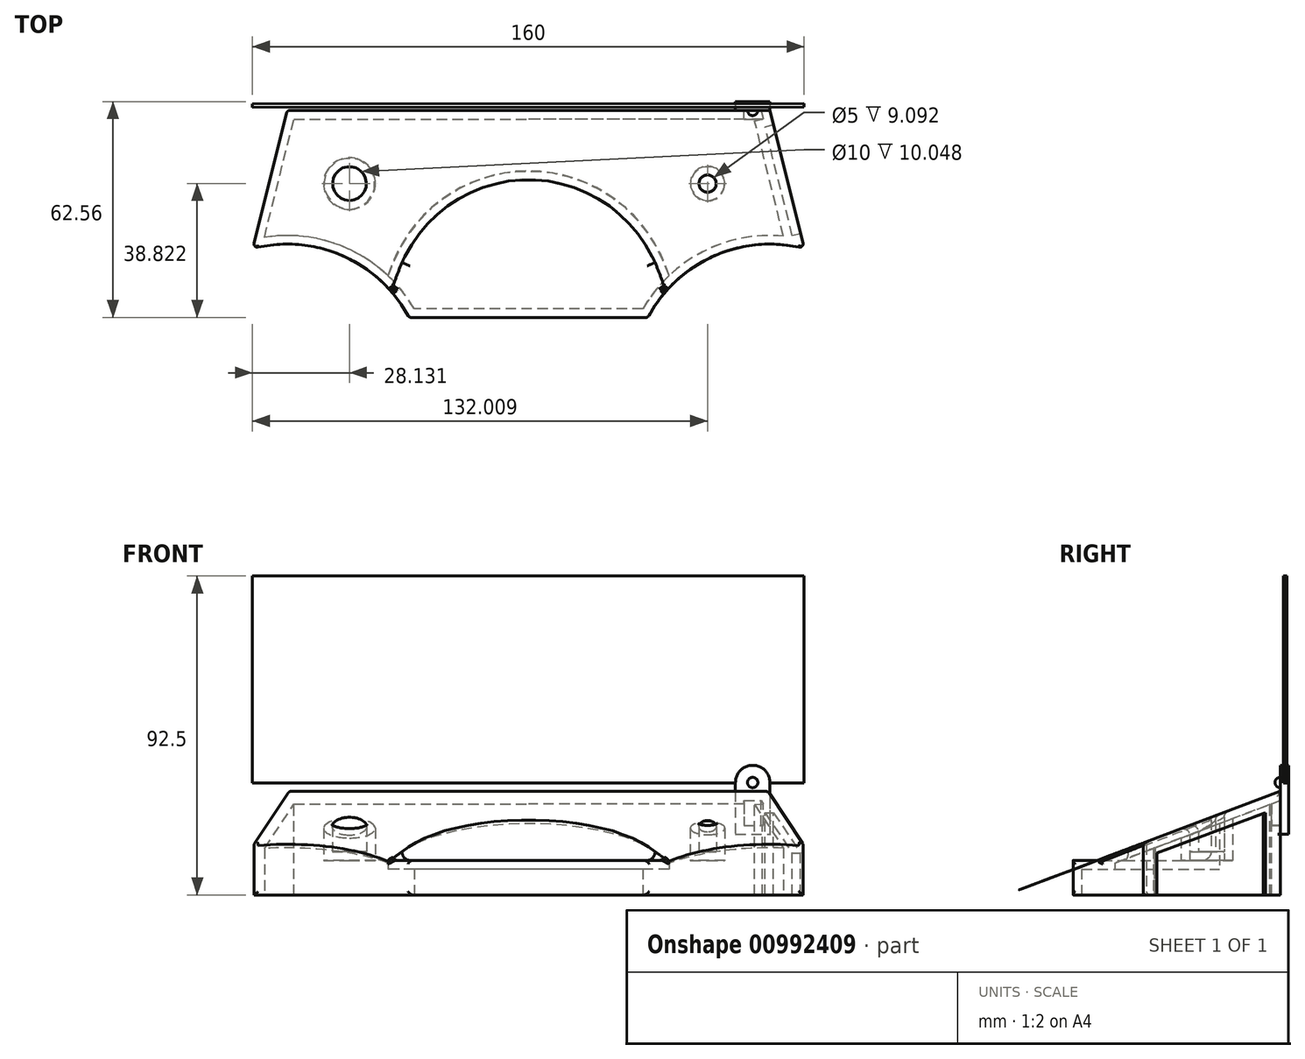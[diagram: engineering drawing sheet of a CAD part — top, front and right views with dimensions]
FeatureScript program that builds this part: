
annotation { "Feature Type Name" : "Feature", "Feature Type Description" : "" }
export const myFeature = defineFeature(function(context is Context, id is Id, definition is map)
    precondition{}
    {
        {
            var Q0;
            Q0=qCreatedBy(makeId("Top.planeOp"),FACE);
            var sketch = newSketch(context, id + "F0", { "sketchPlane" : qUnion([Q0])});
            skLineSegment(sketch, "E0.left", {"start": v(-80, 40) * mm, "end": v(-70, 80.06) * mm});
            skLineSegment(sketch, "E1", {"start": v(0, 0) * mm, "end": v(0, 40) * mm});
            skLineSegment(sketch, "E2", {"start": v(0, 0) * mm, "end": v(0, 80) * mm});
            skLineSegment(sketch, "E3", {"start": v(-70, 80.06) * mm, "end": v(0, 80) * mm});
            skLineSegment(sketch, "E4.MirrorCS", {"start": v(70, 80.06) * mm, "end": v(0, 80) * mm});
            skLineSegment(sketch, "E5.MirrorCS", {"start": v(80, 40) * mm, "end": v(70, 80.06) * mm});
            skCircle(sketch, "E6", {"center": v(0, 40) * mm, "radius": 40 * mm});
            skLineSegment(sketch, "E7", {"start": v(0, 40) * mm, "end": v(0, 0) * mm});
            skLineSegment(sketch, "E8", {"start": v(0, 20) * mm, "end": v(-34.64, 20) * mm});
            skLineSegment(sketch, "E9", {"start": v(-34.64, 20) * mm, "end": v(34.64, 20) * mm});
            skArc(sketch, "E10", {"start": v(-34.64, 20) * mm, "mid": v(-53.85, 37.87) * mm, "end": v(-80, 40) * mm});
            skArc(sketch, "E11", {"start": v(80, 40) * mm, "mid": v(53.85, 37.87) * mm, "end": v(34.64, 20) * mm});
            skSolve(sketch);
        }
        {
            var Q0;
            Q0=makeQuery(id+"F0.imprint","IMPRINT",FACE,{"disambiguationData":[TD([[makeQuery(id+"F0.imprint","IMPRINT",EDGE,{"derivedFrom":sQuery(id+"F0.wireOp",EDGE,"E0.left")}),-1.0]])]});
            var Q1;
            {var subQ0=sQuery(id+"F0.wireOp",EDGE,"E4.MirrorCS");Q1=makeQuery(id+"F0.imprint","IMPRINT",FACE,{"disambiguationData":[TD([[makeQuery(id+"F0.imprint","IMPRINT",EDGE,{"derivedFrom":subQ0}),1.0]])]});}
            var Q2;
            {var subQ6=sQuery(id+"F0.wireOp",EDGE,"E2");Q2=makeQuery(id+"F0.imprint","IMPRINT",FACE,{"disambiguationData":[TD([[makeQuery(id+"F0.imprint","IMPRINT",EDGE,{"derivedFrom":subQ6}),1.0]])]});}
            var Q3;
            {var subQ0=sQuery(id+"F0.wireOp",EDGE,"E7");var subQ1=sQuery(id+"F0.wireOp",EDGE,"E6");var subQ2=makeQuery(id+"F0.imprint","INTERSECT",VERTEX,{"derivedFrom":[subQ1,subQ0]});Q3=makeQuery(id+"F0.imprint","IMPRINT",FACE,{"disambiguationData":[TD([[makeQuery(id+"F0.imprint","IMPRINT",EDGE,{"disambiguationData":[TD([[subQ2,1.0]])],"derivedFrom":subQ0}),-1.0]])]});}
            var Q4;
            {var subQ6=sQuery(id+"F0.wireOp",EDGE,"E2");Q4=makeQuery(id+"F0.imprint","IMPRINT",FACE,{"disambiguationData":[TD([[makeQuery(id+"F0.imprint","IMPRINT",EDGE,{"derivedFrom":subQ6}),-1.0]])]});}
            var Q5;
            {var subQ0=sQuery(id+"F0.wireOp",EDGE,"E7");var subQ1=sQuery(id+"F0.wireOp",EDGE,"E6");var subQ2=makeQuery(id+"F0.imprint","INTERSECT",VERTEX,{"derivedFrom":[subQ1,subQ0]});Q5=makeQuery(id+"F0.imprint","IMPRINT",FACE,{"disambiguationData":[TD([[makeQuery(id+"F0.imprint","IMPRINT",EDGE,{"disambiguationData":[TD([[subQ2,1.0]])],"derivedFrom":subQ0}),1.0]])]});}
            extrude(context, id + "F1", {"entities" : qUnion([Q0, Q1, Q2, Q3, Q4, Q5]), "depth" : 30 * mm, "offsetDistance" : 25 * mm});
        }
        {
            var Q0;
            Q0=qCreatedBy(makeId("Right.planeOp"),FACE);
            var sketch = newSketch(context, id + "F2", { "sketchPlane" : qUnion([Q0])});
            skLineSegment(sketch, "E12", {"start": v(0, 0) * mm, "end": v(0, 10) * mm});
            skLineSegment(sketch, "E13", {"start": v(0, 10) * mm, "end": v(40, 10) * mm});
            skLineSegment(sketch, "E14", {"start": v(40, 10) * mm, "end": v(40, 30) * mm});
            skLineSegment(sketch, "E15", {"start": v(40, 30) * mm, "end": v(0, 30) * mm});
            skLineSegment(sketch, "E16", {"start": v(0, 30) * mm, "end": v(0, 10) * mm});
            skLineSegment(sketch, "E17", {"start": v(0, 30) * mm, "end": v(-10, 30) * mm});
            skLineSegment(sketch, "E18", {"start": v(-10, 30) * mm, "end": v(-10, 10) * mm});
            skLineSegment(sketch, "E19", {"start": v(-10, 10) * mm, "end": v(0, 10) * mm});
            skSolve(sketch);
        }
        {
            var Q0;
            Q0=qSketchRegion(id+"F2",true);
            extrude(context, id + "F3", {"entities" : qUnion([Q0]), "operationType" : NewBodyOperationType.REMOVE, "depth" : 10 * mm, "offsetDistance" : 25 * mm, "hasSecondDirection" : true, "secondDirectionOppositeDirection" : true, "secondDirectionDepth" : 10 * mm});
        }
        {
            var Q0;
            Q0=makeQuery(id+"F1.opExtrude","SWEPT_FACE",FACE,{"disambiguationData":[OSD([sQuery(id+"F0.wireOp",EDGE,"E4.MirrorCS")])]});
            var sketch = newSketch(context, id + "F4", { "sketchPlane" : qUnion([Q0])});
            skLineSegment(sketch, "E20", {"start": v(-0.08, 27.6) * mm, "end": v(-65.08, 27.6) * mm});
            skLineSegment(sketch, "E21.bottom", {"start": v(-65.08, 37.6) * mm, "end": v(-65.08, 37.6) * mm});
            skLineSegment(sketch, "E21.top", {"start": v(-60.08, 17.6) * mm, "end": v(-70.08, 17.6) * mm});
            skLineSegment(sketch, "E21.left", {"start": v(-60.08, 32.6) * mm, "end": v(-60.08, 17.6) * mm});
            skLineSegment(sketch, "E21.right", {"start": v(-70.08, 32.6) * mm, "end": v(-70.08, 17.6) * mm});
            skPoint(sketch, "E21.middle", {"position": v(-65.08, 27.6) * mm});
            skPoint(sketch, "E22.visualSharp", {"position": v(-60.08, 37.6) * mm});
            skArc(sketch, "E22.filletArc", {"start": v(-60.08, 32.6) * mm, "mid": v(-61.55, 36.14) * mm, "end": v(-65.08, 37.6) * mm});
            skPoint(sketch, "E23.visualSharp", {"position": v(-70.08, 37.6) * mm});
            skArc(sketch, "E23.filletArc", {"start": v(-65.08, 37.6) * mm, "mid": v(-68.62, 36.14) * mm, "end": v(-70.08, 32.6) * mm});
            skSolve(sketch);
        }
        {
            var Q0;
            Q0=qSketchRegion(id+"F4",true);
            extrude(context, id + "F5", {"entities" : qUnion([Q0]), "operationType" : NewBodyOperationType.ADD, "depth" : 2.5 * mm, "offsetDistance" : 25 * mm});
        }
        {
            var Q0;
            Q0=makeQuery(id+"F5.opExtrude","CAP_FACE",FACE,{"disambiguationData":[OSD([sQuery(id+"F4.wireOp",EDGE,"E21.top"),sQuery(id+"F4.wireOp",EDGE,"E21.left"),sQuery(id+"F4.wireOp",EDGE,"E21.right"),sQuery(id+"F4.wireOp",EDGE,"E22.filletArc"),sQuery(id+"F4.wireOp",EDGE,"E23.filletArc")])],"isStart":true});
            var sketch = newSketch(context, id + "F6", { "sketchPlane" : qUnion([Q0])});
            skArc(sketch, "E24", {"start": v(66.58, 32.6) * mm, "mid": v(65.08, 34.1) * mm, "end": v(63.58, 32.6) * mm});
            skLineSegment(sketch, "E25", {"start": v(66.58, 32.6) * mm, "end": v(63.58, 32.6) * mm});
            skSolve(sketch);
        }
        {
            var Q0;
            Q0=qSketchRegion(id+"F6",true);
            var Q1;
            Q1=sQuery(id+"F6.wireOp",EDGE,"E25");
            revolve(context, id + "F7", {"operationType" : NewBodyOperationType.ADD, "surfaceOperationType" : NewSurfaceOperationType.NEW, "entities" : qUnion([Q0]), "axis" : qUnion([Q1]), "revolveType" : RevolveType.FULL});
        }
        {
            var Q0;
            Q0=makeQuery(id+"F5.opExtrude","CAP_FACE",FACE,{"disambiguationData":[OSD([sQuery(id+"F4.wireOp",EDGE,"E21.top"),sQuery(id+"F4.wireOp",EDGE,"E21.left"),sQuery(id+"F4.wireOp",EDGE,"E21.right"),sQuery(id+"F4.wireOp",EDGE,"E22.filletArc"),sQuery(id+"F4.wireOp",EDGE,"E23.filletArc")])],"isStart":false});
            cPlane(context, id + "F8", {"entities" : qUnion([Q0]), "cplaneType" : CPlaneType.OFFSET, "offset" : 1 * mm, "oppositeDirection" : true, "width" : 150 * mm, "height" : 150 * mm});
        }
        {
            var Q0;
            Q0=qCreatedBy(id+"F8.planeOp",FACE);
            var sketch = newSketch(context, id + "F9", { "sketchPlane" : qUnion([Q0])});
            skLineSegment(sketch, "E26", {"start": v(0, 0) * mm, "end": v(0, 32.5) * mm});
            skLineSegment(sketch, "E27", {"start": v(0, 32.5) * mm, "end": v(-80, 32.5) * mm});
            skLineSegment(sketch, "E28", {"start": v(-80, 32.5) * mm, "end": v(-80, 92.5) * mm});
            skLineSegment(sketch, "E29", {"start": v(-80, 92.5) * mm, "end": v(0, 92.5) * mm});
            skLineSegment(sketch, "E30", {"start": v(0, 92.5) * mm, "end": v(80, 92.5) * mm});
            skLineSegment(sketch, "E31", {"start": v(80, 92.5) * mm, "end": v(80, 32.5) * mm});
            skLineSegment(sketch, "E32", {"start": v(80, 32.5) * mm, "end": v(0, 32.5) * mm});
            skSolve(sketch);
        }
        {
            var Q0;
            Q0=qSketchRegion(id+"F9",true);
            extrude(context, id + "F10", {"entities" : qUnion([Q0]), "operationType" : NewBodyOperationType.ADD, "depth" : 0.5 * mm, "offsetDistance" : 25 * mm, "hasSecondDirection" : true, "secondDirectionOppositeDirection" : true, "secondDirectionDepth" : 0.5 * mm});
        }
        {
            var Q0;
            Q0=makeQuery(id+"F3.boolean.opBoolean","COPY",FACE,{"derivedFrom":makeQuery(id+"F3.opExtrude","SWEPT_FACE",FACE,{"disambiguationData":[OSD([sQuery(id+"F2.wireOp",EDGE,"E13"),sQuery(id+"F2.wireOp",EDGE,"E19")])]})});
            var sketch = newSketch(context, id + "F11", { "sketchPlane" : qUnion([Q0])});
            skLineSegment(sketch, "E33", {"start": v(0, 0) * mm, "end": v(0, 40) * mm});
            skPoint(sketch, "E33.endSnap0", {"position": v(0, 40) * mm});
            skCircle(sketch, "E34", {"center": v(0, 20) * mm, "radius": 40 * mm});
            skSolve(sketch);
        }
        {
            var Q0;
            Q0 = qSketchRegion(id + "F11", true);
            extrude(context, id + "F12", {"entities" : qUnion([Q0]), "operationType" : NewBodyOperationType.REMOVE, "endBound" : BoundingType.THROUGH_ALL, "depth" : 25 * mm, "offsetDistance" : 25 * mm});
        }
        {
            var Q0;
            Q0=qCreatedBy(makeId("Right.planeOp"),FACE);
            var sketch = newSketch(context, id + "F13", { "sketchPlane" : qUnion([Q0])});
            skLineSegment(sketch, "E35", {"start": v(80, 30) * mm, "end": v(27, 10) * mm});
            skLineSegment(sketch, "E36", {"start": v(27, 10) * mm, "end": v(27, 30) * mm});
            skLineSegment(sketch, "E37", {"start": v(27, 30) * mm, "end": v(80, 30) * mm});
            skSolve(sketch);
        }
        {
            var Q0;
            Q0 = qSketchRegion(id + "F13", true);
            extrude(context, id + "F14", {"entities" : qUnion([Q0]), "operationType" : NewBodyOperationType.REMOVE, "endBound" : BoundingType.THROUGH_ALL, "oppositeDirection" : true, "depth" : 25 * mm, "offsetDistance" : 25 * mm, "hasSecondDirection" : true, "secondDirectionBound" : SecondDirectionBoundingType.THROUGH_ALL, "secondDirectionOppositeDirection" : false, "secondDirectionDepth" : 25 * mm});
        }
        {
            var Q0;
            Q0=makeQuery(id+"F1.opExtrude","SWEPT_FACE",FACE,{"disambiguationData":[OSD([sQuery(id+"F0.wireOp",EDGE,"E5.MirrorCS")])]});
            var sketch = newSketch(context, id + "F15", { "sketchPlane" : qUnion([Q0])});
            skLineSegment(sketch, "E38", {"start": v(19.43, 0) * mm, "end": v(60.72, 0) * mm});
            skLineSegment(sketch, "E39.bottom", {"start": v(56.32, -12.08) * mm, "end": v(23.82, -12.08) * mm});
            skLineSegment(sketch, "E39.left", {"start": v(56.32, -12.08) * mm, "end": v(56.32, 12.08) * mm});
            skLineSegment(sketch, "E39.right", {"start": v(23.82, -12.08) * mm, "end": v(23.82, 12.08) * mm});
            skPoint(sketch, "E39.middle", {"position": v(40.07, 0) * mm});
            skLineSegment(sketch, "E40", {"start": v(56.32, 12.08) * mm, "end": v(56.32, 23.8) * mm});
            skLineSegment(sketch, "E41", {"start": v(56.32, 23.8) * mm, "end": v(23.82, 12.08) * mm});
            skSolve(sketch);
        }
        {
            var Q0;
            Q0 = qSketchRegion(id + "F15", true);
            extrude(context, id + "F16", {"entities" : qUnion([Q0]), "operationType" : NewBodyOperationType.REMOVE, "oppositeDirection" : true, "depth" : 2.5 * mm, "offsetDistance" : 25 * mm});
        }
        {
            var Q0;
            Q0=makeQuery(id+"F1.opExtrude","SWEPT_FACE",FACE,{"disambiguationData":[OSD([sQuery(id+"F0.wireOp",EDGE,"E11")])]});
            var Q1;
            Q1=makeQuery(id+"F12.boolean.opBoolean","INTERSECT",EDGE,{"derivedFrom":[makeQuery(id+"F1.opExtrude","SWEPT_FACE",FACE,{"disambiguationData":[OSD([sQuery(id+"F0.wireOp",EDGE,"E6")])]}),makeQuery(id+"F12.opExtrude","CAP_FACE",FACE,{"disambiguationData":[OSD([sQuery(id+"F11.wireOp",EDGE,"E34")])],"isStart":true})]});
            var Q2;
            Q2=makeQuery(id+"F1.opExtrude","SWEPT_FACE",FACE,{"disambiguationData":[OSD([sQuery(id+"F0.wireOp",EDGE,"E10")])]});
            var Q3;
            Q3=makeQuery(id+"F1.opExtrude","SWEPT_FACE",FACE,{"disambiguationData":[OSD([sQuery(id+"F0.wireOp",EDGE,"E6")])]});
            var Q4;
            Q4=makeQuery(id+"F14.boolean.opBoolean","INTERSECT",EDGE,{"derivedFrom":[makeQuery(id+"F1.opExtrude","SWEPT_FACE",FACE,{"disambiguationData":[OSD([sQuery(id+"F0.wireOp",EDGE,"E5.MirrorCS")])]}),makeQuery(id+"F14.opExtrude","SWEPT_FACE",FACE,{"disambiguationData":[OSD([sQuery(id+"F13.wireOp",EDGE,"E35")])]})]});
            var Q5;
            Q5=makeQuery(id+"F16.boolean.opBoolean","COPY",EDGE,{"derivedFrom":makeQuery(id+"F16.opExtrude","CAP_EDGE",EDGE,{"disambiguationData":[OSD([sQuery(id+"F15.wireOp",EDGE,"E39.right")])],"isStart":true})});
            var Q6;
            Q6=makeQuery(id+"F16.boolean.opBoolean","COPY",EDGE,{"derivedFrom":makeQuery(id+"F16.opExtrude","CAP_EDGE",EDGE,{"disambiguationData":[OSD([sQuery(id+"F15.wireOp",EDGE,"E41")])],"isStart":true})});
            var Q7;
            Q7=makeQuery(id+"F16.boolean.opBoolean","COPY",EDGE,{"derivedFrom":makeQuery(id+"F16.opExtrude","CAP_EDGE",EDGE,{"disambiguationData":[OSD([sQuery(id+"F15.wireOp",EDGE,"E39.left"),sQuery(id+"F15.wireOp",EDGE,"E40")])],"isStart":true})});
            var Q8;
            {var subQ0=sQuery(id+"F0.wireOp",EDGE,"E4.MirrorCS");var subQ1=sQuery(id+"F0.wireOp",EDGE,"E5.MirrorCS");Q8=makeQuery(id+"F5.boolean.opBoolean","SPLIT",EDGE,{"disambiguationData":[topologyDisambiguationEdgeConnected([makeQuery(id+"F1.opExtrude","SWEPT_FACE",FACE,{"disambiguationData":[OSD([subQ0])]})])],"derivedFrom":makeQuery(id+"F1.opExtrude","SWEPT_EDGE",EDGE,{"disambiguationData":[OSD([subQ0,subQ1])]})});}
            var Q9;
            Q9=makeQuery(id+"F14.boolean.opBoolean","INTERSECT",EDGE,{"derivedFrom":[makeQuery(id+"F1.opExtrude","SWEPT_FACE",FACE,{"disambiguationData":[OSD([sQuery(id+"F0.wireOp",EDGE,"E0.left")])]}),makeQuery(id+"F14.opExtrude","SWEPT_FACE",FACE,{"disambiguationData":[OSD([sQuery(id+"F13.wireOp",EDGE,"E35")])]})]});
            var Q10;
            Q10=makeQuery(id+"FMOqGt4334W161Y_1.1.F16.boolean.opBoolean","COPY",EDGE,{"derivedFrom":makeQuery(id+"FMOqGt4334W161Y_1.1.F16.opExtrude","CAP_EDGE",EDGE,{"disambiguationData":[OSD([sQuery(id+"F15.wireOp",EDGE,"E41")])],"isStart":true})});
            var Q11;
            Q11=makeQuery(id+"FMOqGt4334W161Y_1.1.F16.boolean.opBoolean","COPY",EDGE,{"derivedFrom":makeQuery(id+"FMOqGt4334W161Y_1.1.F16.opExtrude","CAP_EDGE",EDGE,{"disambiguationData":[OSD([sQuery(id+"F15.wireOp",EDGE,"E39.left"),sQuery(id+"F15.wireOp",EDGE,"E40")])],"isStart":true})});
            var Q12;
            {var subQ0=sQuery(id+"F0.wireOp",EDGE,"E0.left");var subQ1=sQuery(id+"F0.wireOp",EDGE,"E3");Q12=makeQuery(id+"FqNquMD9BT1ISZJ_1.1.F5.boolean.opBoolean","SPLIT",EDGE,{"disambiguationData":[topologyDisambiguationEdgeConnected([makeQuery(id+"F1.opExtrude","SWEPT_FACE",FACE,{"disambiguationData":[OSD([subQ1])]})])],"derivedFrom":makeQuery(id+"F1.opExtrude","SWEPT_EDGE",EDGE,{"disambiguationData":[OSD([subQ0,subQ1])]})});}
            var Q13;
            Q13=makeQuery(id+"FMOqGt4334W161Y_1.1.F16.boolean.opBoolean","COPY",EDGE,{"derivedFrom":makeQuery(id+"FMOqGt4334W161Y_1.1.F16.opExtrude","CAP_EDGE",EDGE,{"disambiguationData":[OSD([sQuery(id+"F15.wireOp",EDGE,"E39.right")])],"isStart":true})});
            fillet(context, id + "F17", {"entities" : qUnion([Q0, Q1, Q2, Q3, Q4, Q5, Q6, Q7, Q8, Q9, Q10, Q11, Q12, Q13]), "radius" : 1 * mm, "tangentPropagation" : true, "allowEdgeOverflow" : false});
        }
        {
            var Q0;
            Q0=qCreatedBy(makeId("Top.planeOp"),FACE);
            cPlane(context, id + "F18", {"entities" : qUnion([Q0]), "cplaneType" : CPlaneType.OFFSET, "offset" : 12.5 * mm, "width" : 150 * mm, "height" : 150 * mm});
        }
        {
            var Q0;
            Q0=qCreatedBy(id+"F18.planeOp",FACE);
            var sketch = newSketch(context, id + "F19", { "sketchPlane" : qUnion([Q0])});
            skCircle(sketch, "E42", {"center": v(-51.94, 58.82) * mm, "radius": 5 * mm});
            skCircle(sketch, "E43", {"center": v(51.94, 58.82) * mm, "radius": 2.5 * mm});
            skSolve(sketch);
        }
        {
            var Q0;
            Q0 = qSketchRegion(id + "F19", true);
            extrude(context, id + "F20", {"entities" : qUnion([Q0]), "operationType" : NewBodyOperationType.REMOVE, "depth" : 25 * mm, "offsetDistance" : 25 * mm});
        }
        {
            var Q0;
            Q0=makeQuery(id+"F1.opExtrude","CAP_FACE",FACE,{"disambiguationData":[OSD([sQuery(id+"F0.wireOp",EDGE,"E0.left"),sQuery(id+"F0.wireOp",EDGE,"E3"),sQuery(id+"F0.wireOp",EDGE,"E4.MirrorCS"),sQuery(id+"F0.wireOp",EDGE,"E5.MirrorCS"),sQuery(id+"F0.wireOp",EDGE,"E6"),sQuery(id+"F0.wireOp",EDGE,"E10"),sQuery(id+"F0.wireOp",EDGE,"E11")])],"isStart":true});
            shell(context, id + "F21", {"entities" : qUnion([Q0]), "thickness" : 2.5 * mm});
        }
        {
            var Q0;
            Q0=makeQuery(id+"F14.boolean.opBoolean","INTERSECT",EDGE,{"derivedFrom":[makeQuery(id+"F12.boolean.opBoolean","COPY",FACE,{"derivedFrom":makeQuery(id+"F12.opExtrude","SWEPT_FACE",FACE,{"disambiguationData":[OSD([sQuery(id+"F11.wireOp",EDGE,"E34")])]})}),makeQuery(id+"F14.opExtrude","SWEPT_FACE",FACE,{"disambiguationData":[OSD([sQuery(id+"F13.wireOp",EDGE,"E35")])]})]});
            fillet(context, id + "F22", {"entities" : qUnion([Q0]), "radius" : 0.95 * mm, "tangentPropagation" : true, "allowEdgeOverflow" : false});
        }
        {
            var Q0;
            Q0=makeQuery(id+"F20.boolean.opBoolean","INTERSECT",EDGE,{"derivedFrom":[makeQuery(id+"F14.boolean.opBoolean","COPY",FACE,{"derivedFrom":makeQuery(id+"F14.opExtrude","SWEPT_FACE",FACE,{"disambiguationData":[OSD([sQuery(id+"F13.wireOp",EDGE,"E35")])]})}),makeQuery(id+"F20.opExtrude","SWEPT_FACE",FACE,{"disambiguationData":[OSD([sQuery(id+"F19.wireOp",EDGE,"E42")])]})]});
            var Q1;
            Q1=makeQuery(id+"F20.boolean.opBoolean","INTERSECT",EDGE,{"derivedFrom":[makeQuery(id+"F14.boolean.opBoolean","COPY",FACE,{"derivedFrom":makeQuery(id+"F14.opExtrude","SWEPT_FACE",FACE,{"disambiguationData":[OSD([sQuery(id+"F13.wireOp",EDGE,"E35")])]})}),makeQuery(id+"F20.opExtrude","SWEPT_FACE",FACE,{"disambiguationData":[OSD([sQuery(id+"F19.wireOp",EDGE,"E43")])]})]});
            fillet(context, id + "F23", {"entities" : qUnion([Q0, Q1]), "radius" : 2 * mm, "tangentPropagation" : true, "allowEdgeOverflow" : false});
        }
        {
            var Q0;
            Q0=makeQuery(id+"F12.boolean.opBoolean","COPY",EDGE,{"derivedFrom":makeQuery(id+"F12.opExtrude","CAP_EDGE",EDGE,{"disambiguationData":[OSD([sQuery(id+"F11.wireOp",EDGE,"E34")])],"isStart":true})});
            fillet(context, id + "F24", {"entities" : qUnion([Q0]), "radius" : 2.5 * mm, "tangentPropagation" : true, "allowEdgeOverflow" : false});
        }
    });
